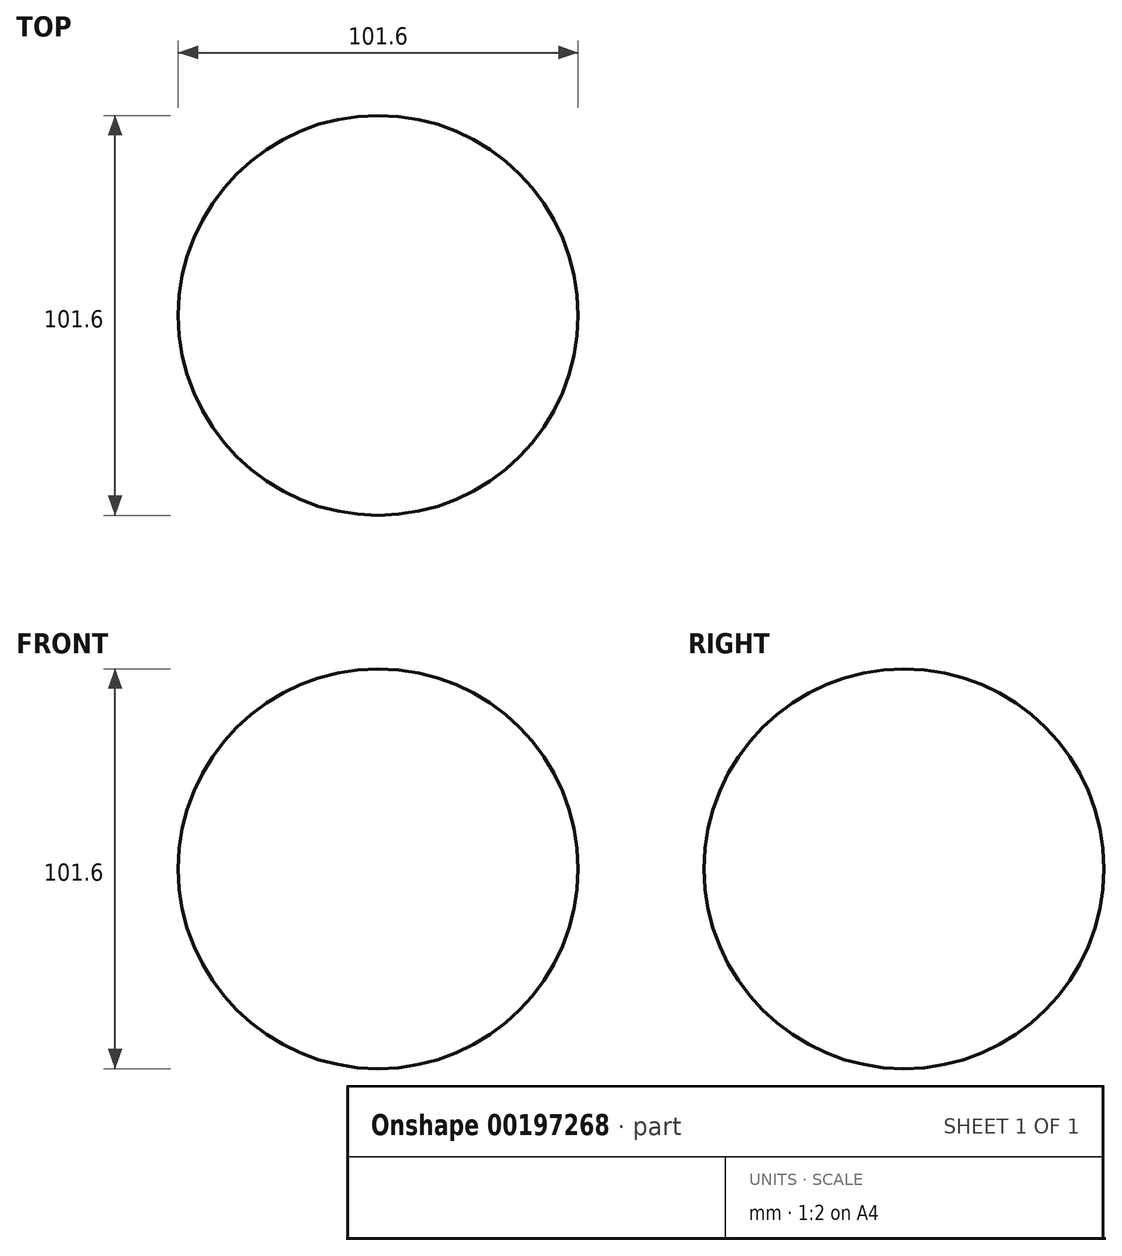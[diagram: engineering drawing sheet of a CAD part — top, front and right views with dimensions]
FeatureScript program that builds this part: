
annotation { "Feature Type Name" : "Feature", "Feature Type Description" : "" }
export const myFeature = defineFeature(function(context is Context, id is Id, definition is map)
    precondition{}
    {
        {
            var Q0;
            Q0=qCreatedBy(makeId("Top.planeOp"),FACE);
            var sketch = newSketch(context, id + "F0", { "sketchPlane" : qUnion([Q0])});
            skCircle(sketch, "E0", {"center": v(0, 0) * mm, "radius": 50.8 * mm});
            skLineSegment(sketch, "E1", {"start": v(0, 0) * mm, "end": v(0, -50.8) * mm});
            skLineSegment(sketch, "E2", {"start": v(0, 0) * mm, "end": v(0, 50.8) * mm});
            skSolve(sketch);
        }
        {
            var Q0;
            {var subQ0=sQuery(id+"F0.wireOp",EDGE,"E1");Q0=makeQuery(id+"F0.imprint","IMPRINT",FACE,{"disambiguationData":[TD([[makeQuery(id+"F0.imprint","IMPRINT",EDGE,{"derivedFrom":subQ0}),-1.0]])]});}
            var Q1;
            Q1=sQuery(id+"F0.wireOp",EDGE,"E2");
            revolve(context, id + "F1", {"entities" : qUnion([Q0]), "axis" : qUnion([Q1]), "revolveType" : RevolveType.FULL});
        }
    });
